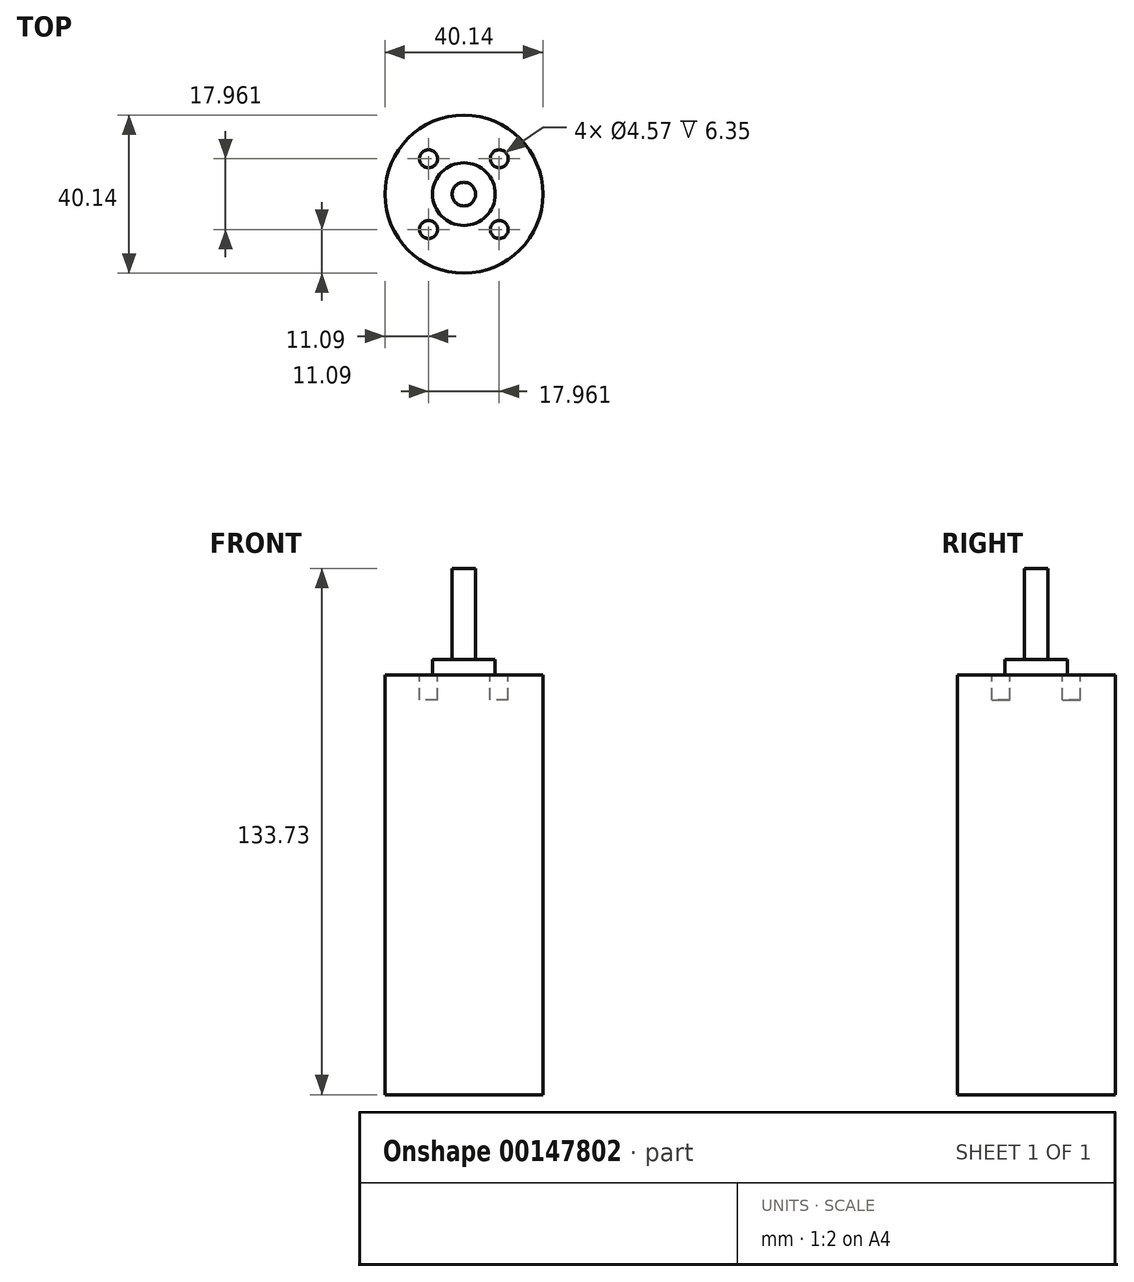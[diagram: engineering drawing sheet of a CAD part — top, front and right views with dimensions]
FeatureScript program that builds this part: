
annotation { "Feature Type Name" : "Feature", "Feature Type Description" : "" }
export const myFeature = defineFeature(function(context is Context, id is Id, definition is map)
    precondition{}
    {
        {
            var Q0;
            Q0=qCreatedBy(makeId("Top.planeOp"),FACE);
            var sketch = newSketch(context, id + "F0", { "sketchPlane" : qUnion([Q0])});
            skCircle(sketch, "E0", {"center": v(0, 0) * mm, "radius": 20.07 * mm});
            skSolve(sketch);
        }
        {
            var Q0;
            Q0=qSketchRegion(id+"F0",true);
            extrude(context, id + "F1", {"entities" : qUnion([Q0]), "depth" : 106.68 * mm});
        }
        {
            var Q0;
            Q0=makeQuery(id+"F1.opExtrude","CAP_FACE",FACE,{"disambiguationData":[OSD([sQuery(id+"F0.wireOp",EDGE,"E0")])],"isStart":false});
            var sketch = newSketch(context, id + "F2", { "sketchPlane" : qUnion([Q0])});
            skCircle(sketch, "E1", {"center": v(0, 0) * mm, "radius": 7.96 * mm});
            skSolve(sketch);
        }
        {
            var Q0;
            Q0=qSketchRegion(id+"F2",true);
            extrude(context, id + "F3", {"entities" : qUnion([Q0]), "operationType" : NewBodyOperationType.ADD, "depth" : 3.84 * mm});
        }
        {
            var Q0;
            Q0=makeQuery(id+"F3.opExtrude","CAP_FACE",FACE,{"disambiguationData":[OSD([sQuery(id+"F2.wireOp",EDGE,"E1")])],"isStart":false});
            var sketch = newSketch(context, id + "F4", { "sketchPlane" : qUnion([Q0])});
            skCircle(sketch, "E2", {"center": v(0, 0) * mm, "radius": 3 * mm});
            skSolve(sketch);
        }
        {
            var Q0;
            Q0=makeQuery(id+"F1.opExtrude","CAP_FACE",FACE,{"disambiguationData":[OSD([sQuery(id+"F0.wireOp",EDGE,"E0")])],"isStart":false});
            var sketch = newSketch(context, id + "F5", { "sketchPlane" : qUnion([Q0])});
            skLineSegment(sketch, "E3.bottom", {"start": v(-8.98, -8.98) * mm, "end": v(8.98, -8.98) * mm, "construction": true});
            skLineSegment(sketch, "E3.top", {"start": v(-8.98, 8.98) * mm, "end": v(8.98, 8.98) * mm, "construction": true});
            skLineSegment(sketch, "E3.left", {"start": v(-8.98, -8.98) * mm, "end": v(-8.98, 8.98) * mm, "construction": true});
            skLineSegment(sketch, "E3.right", {"start": v(8.98, -8.98) * mm, "end": v(8.98, 8.98) * mm, "construction": true});
            skPoint(sketch, "E3.middle", {"position": v(0, 0) * mm});
            skLineSegment(sketch, "E4", {"start": v(0, 0) * mm, "end": v(-8.98, 8.98) * mm, "construction": true});
            skCircle(sketch, "E5", {"center": v(-8.98, 8.98) * mm, "radius": 2.29 * mm});
            skCircle(sketch, "E6", {"center": v(-8.98, -8.98) * mm, "radius": 2.29 * mm});
            skCircle(sketch, "E7", {"center": v(8.98, -8.98) * mm, "radius": 2.29 * mm});
            skCircle(sketch, "E8", {"center": v(8.98, 8.98) * mm, "radius": 2.29 * mm});
            skSolve(sketch);
        }
        {
            var Q0;
            Q0=qSketchRegion(id+"F5",true);
            extrude(context, id + "F6", {"entities" : qUnion([Q0]), "operationType" : NewBodyOperationType.REMOVE, "oppositeDirection" : true, "depth" : 6.35 * mm});
        }
        {
            var Q0;
            Q0=qSketchRegion(id+"F4",true);
            extrude(context, id + "F7", {"entities" : qUnion([Q0]), "operationType" : NewBodyOperationType.ADD, "depth" : 23.22 * mm});
        }
    });
